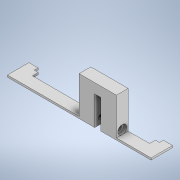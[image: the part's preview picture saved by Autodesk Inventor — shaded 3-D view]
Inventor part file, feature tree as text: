
AUTODESK INVENTOR PART (.ipt)
format: ipt  version: 2020 (Build 240168000, 168)  size: 156,672 bytes
history: native  units: mm
features: sketch x4, extrude x3, hole x1
ambient origin geometry x8: Origin, YZ Plane, XZ Plane, XY Plane, X Axis, Y Axis, Z Axis, Center Point
bodies: Solid1 (feature_tree)
feature tree (8):
  extrude  "Extrusion1"  Depth=20.0mm TaperAngle=0.0deg
  extrude  "Extrusion2"  Depth=5.0mm
  extrude  "Extrusion3"  Depth=6.0mm
  hole  "Hole1"  [1 undecoded]
  sketch  "Sketch1"  dims[d0=18.92mm d1=3.15mm d2=8.0mm d3=8.0mm d4=20.0mm d5=0.0mm]
  sketch  "Sketch2"  dims[d6=1.0mm d7=0.0mm d8=5.0mm]
  sketch  "Sketch3"  dims[d9=5.5mm d10=0.0mm d11=6.0mm]
  sketch  "Sketch4"  dims[d12=3.0mm d13=2.2mm d14=2.4mm d15=6.0mm d16=4.6mm d17=1.5mm d18=90.0deg d19=24.0mm d20=20.594885mm]
note: 1 required parameter value undecoded (feature->parameter linkage not recoverable at this tier; creation-order binding heuristic only, values carry confidence <= 0.55)
